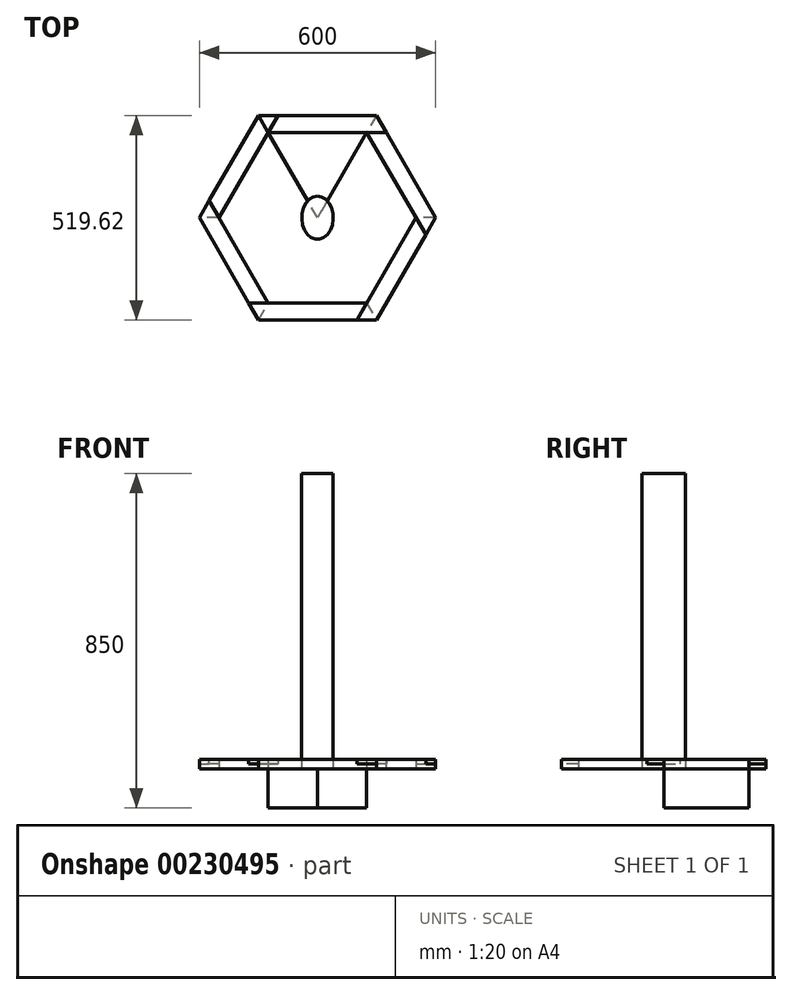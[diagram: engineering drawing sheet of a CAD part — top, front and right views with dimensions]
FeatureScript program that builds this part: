
annotation { "Feature Type Name" : "Feature", "Feature Type Description" : "" }
export const myFeature = defineFeature(function(context is Context, id is Id, definition is map)
    precondition{}
    {
        {
            var Q0;
            Q0=qCreatedBy(makeId("Top.planeOp"),FACE);
            var sketch = newSketch(context, id + "F0", { "sketchPlane" : qUnion([Q0])});
            skLineSegment(sketch, "E0", {"start": v(0, 0) * mm, "end": v(300, 0) * mm});
            skLineSegment(sketch, "E1", {"start": v(-24.83, 43) * mm, "end": v(275.17, 43) * mm});
            skLineSegment(sketch, "E2", {"start": v(0, 0) * mm, "end": v(-24.83, 43) * mm});
            skLineSegment(sketch, "E3", {"start": v(300, 0) * mm, "end": v(275.17, 43) * mm});
            skSolve(sketch);
        }
        {
            var Q0;
            Q0 = qSketchRegion(id + "F0", true);
            extrude(context, id + "F1", {"entities" : qUnion([Q0]), "depth" : 23 * mm});
        }
        {
            var Q0;
            Q0=makeQuery(id+"F1.opExtrude","CAP_FACE",FACE,{"disambiguationData":[OSD([sQuery(id+"F0.wireOp",EDGE,"E0"),sQuery(id+"F0.wireOp",EDGE,"E1"),sQuery(id+"F0.wireOp",EDGE,"E2"),sQuery(id+"F0.wireOp",EDGE,"E3")])],"isStart":false});
            var sketch = newSketch(context, id + "F2", { "sketchPlane" : qUnion([Q0])});
            skLineSegment(sketch, "E4", {"start": v(0, 0) * mm, "end": v(24.83, 43) * mm});
            skLineSegment(sketch, "E5", {"start": v(24.83, 43) * mm, "end": v(-24.83, 43) * mm});
            skLineSegment(sketch, "E6", {"start": v(-24.83, 43) * mm, "end": v(0, 0) * mm});
            skSolve(sketch);
        }
        {
            var Q0;
            Q0=makeQuery(id+"F2.imprint","IMPRINT",FACE,{"disambiguationData":[TD([[makeQuery(id+"F2.imprint","IMPRINT",EDGE,{"derivedFrom":sQuery(id+"F2.wireOp",EDGE,"E4")}),1.0]])]});
            extrude(context, id + "F3", {"entities" : qUnion([Q0]), "operationType" : NewBodyOperationType.REMOVE, "oppositeDirection" : true, "depth" : 11.5 * mm});
        }
        {
            var Q0;
            Q0=makeQuery(id+"F1.opExtrude","CAP_FACE",FACE,{"disambiguationData":[OSD([sQuery(id+"F0.wireOp",EDGE,"E0"),sQuery(id+"F0.wireOp",EDGE,"E1"),sQuery(id+"F0.wireOp",EDGE,"E2"),sQuery(id+"F0.wireOp",EDGE,"E3")])],"isStart":true});
            var sketch = newSketch(context, id + "F4", { "sketchPlane" : qUnion([Q0])});
            skLineSegment(sketch, "E7", {"start": v(275.17, -43) * mm, "end": v(250.35, 0) * mm});
            skLineSegment(sketch, "E8", {"start": v(250.35, 0) * mm, "end": v(300, 0) * mm});
            skLineSegment(sketch, "E9", {"start": v(300, 0) * mm, "end": v(275.17, -43) * mm});
            skSolve(sketch);
        }
        {
            var Q0;
            Q0=makeQuery(id+"F4.imprint","IMPRINT",FACE,{"disambiguationData":[TD([[makeQuery(id+"F4.imprint","IMPRINT",EDGE,{"derivedFrom":sQuery(id+"F4.wireOp",EDGE,"E7")}),-1.0]])]});
            extrude(context, id + "F5", {"entities" : qUnion([Q0]), "operationType" : NewBodyOperationType.REMOVE, "oppositeDirection" : true, "depth" : 11.5 * mm});
        }
        {
            var Q0;
            Q0=qCreatedBy(makeId("Top.planeOp"),FACE);
            var sketch = newSketch(context, id + "F6", { "sketchPlane" : qUnion([Q0])});
            skLineSegment(sketch, "E10", {"start": v(0, 0) * mm, "end": v(250.35, 0) * mm});
            skLineSegment(sketch, "E11", {"start": v(250.35, 0) * mm, "end": v(125.17, -216.8) * mm});
            skLineSegment(sketch, "E12", {"start": v(125.17, -216.8) * mm, "end": v(0, 0) * mm});
            skSolve(sketch);
        }
        {
            var Q0;
            Q0 = qSketchRegion(id + "F6", true);
            extrude(context, id + "F7", {"entities" : qUnion([Q0]), "oppositeDirection" : true, "depth" : 100 * mm});
        }
        {
            var Q0;
            Q0=makeQuery(id+"F1.opExtrude","SWEPT_BODY",BODY,{"disambiguationData":[OSD([sQuery(id+"F0.wireOp",EDGE,"E0"),sQuery(id+"F0.wireOp",EDGE,"E1"),sQuery(id+"F0.wireOp",EDGE,"E2"),sQuery(id+"F0.wireOp",EDGE,"E3")])]});
            var Q1;
            Q1=makeQuery(id+"F7.opExtrude","SWEPT_EDGE",EDGE,{"disambiguationData":[OSD([sQuery(id+"F6.wireOp",EDGE,"E11"),sQuery(id+"F6.wireOp",EDGE,"E12")])]});
            circularPattern(context, id + "F8", {"entities" : qUnion([Q0]), "axis" : qUnion([Q1]), "angle" : 360 * degree, "instanceCount" : 6, "equalSpace" : true});
        }
        {
            var Q0;
            Q0=makeQuery(id+"F8.opPattern","COPY",FACE,{"derivedFrom":makeQuery(id+"F1.opExtrude","CAP_FACE",FACE,{"disambiguationData":[OSD([sQuery(id+"F0.wireOp",EDGE,"E0"),sQuery(id+"F0.wireOp",EDGE,"E1"),sQuery(id+"F0.wireOp",EDGE,"E2"),sQuery(id+"F0.wireOp",EDGE,"E3")])],"isStart":true}),"instanceName":"3"});
            var sketch = newSketch(context, id + "F9", { "sketchPlane" : qUnion([Q0])});
            skLineSegment(sketch, "E13", {"start": v(105.17, 476.62) * mm, "end": v(105.17, 228.35) * mm});
            skLineSegment(sketch, "E14", {"start": v(105.17, 476.62) * mm, "end": v(145.17, 476.62) * mm});
            skLineSegment(sketch, "E15", {"start": v(145.17, 476.62) * mm, "end": v(145.17, 228.35) * mm});
            skLineSegment(sketch, "E16", {"start": v(-62.59, 325.21) * mm, "end": v(312.93, 108.4) * mm, "construction": true});
            skLineSegment(sketch, "E17.MirrorCS", {"start": v(-89.83, 69.58) * mm, "end": v(125.17, 193.71) * mm});
            skLineSegment(sketch, "E18.MirrorCS", {"start": v(-109.83, 104.22) * mm, "end": v(-89.83, 69.58) * mm});
            skLineSegment(sketch, "E19.MirrorCS", {"start": v(-109.83, 104.22) * mm, "end": v(105.17, 228.35) * mm});
            skLineSegment(sketch, "E20", {"start": v(-62.59, 108.4) * mm, "end": v(312.93, 325.21) * mm, "construction": true});
            skLineSegment(sketch, "E21.MirrorCS", {"start": v(340.17, 69.58) * mm, "end": v(360.17, 104.22) * mm});
            skLineSegment(sketch, "E22.MirrorCS", {"start": v(340.17, 69.58) * mm, "end": v(125.17, 193.71) * mm});
            skLineSegment(sketch, "E23.MirrorCS", {"start": v(360.17, 104.22) * mm, "end": v(145.17, 228.35) * mm});
            skPoint(sketch, "E24", {"position": v(125.17, 216.8) * mm});
            skLineSegment(sketch, "E25", {"start": v(105.17, 228.35) * mm, "end": v(125.17, 216.8) * mm});
            skLineSegment(sketch, "E26", {"start": v(125.17, 216.8) * mm, "end": v(125.17, 193.71) * mm});
            skLineSegment(sketch, "E27", {"start": v(125.17, 216.8) * mm, "end": v(145.17, 228.35) * mm});
            skEllipse(sketch, "E28", {"center": v(125.17, 216.8) * mm, "majorRadius": 55 * mm, "minorRadius": 40 * mm, "majorAxis": v(0, -1)});
            skLineSegment(sketch, "E29", {"start": v(125.17, 161.8) * mm, "end": v(125.17, 271.8) * mm, "construction": true});
            skLineSegment(sketch, "E30", {"start": v(125.17, 433.62) * mm, "end": v(125.17, 0) * mm, "construction": true});
            skSolve(sketch);
        }
        {
            var Q0;
            {var subQ1=sQuery(id+"F9.wireOp",EDGE,"E13");var subQ3=sQuery(id+"F9.wireOp",EDGE,"E28");var subQ4=makeQuery(id+"F9.imprint","INTERSECT",VERTEX,{"derivedFrom":[subQ1,subQ3]});Q0=makeQuery(id+"F9.imprint","IMPRINT",FACE,{"disambiguationData":[TD([[makeQuery(id+"F9.imprint","IMPRINT",EDGE,{"disambiguationData":[TD([[subQ4,-1.0]])],"derivedFrom":subQ3}),1.0]])]});}
            var Q1;
            {var subQ6=sQuery(id+"F9.wireOp",EDGE,"E25");Q1=makeQuery(id+"F9.imprint","IMPRINT",FACE,{"disambiguationData":[TD([[makeQuery(id+"F9.imprint","IMPRINT",EDGE,{"derivedFrom":subQ6}),1.0]])]});}
            var Q2;
            {var subQ1=sQuery(id+"F9.wireOp",EDGE,"E25");Q2=makeQuery(id+"F9.imprint","IMPRINT",FACE,{"disambiguationData":[TD([[makeQuery(id+"F9.imprint","IMPRINT",EDGE,{"derivedFrom":subQ1}),-1.0]])]});}
            var Q3;
            {var subQ1=sQuery(id+"F9.wireOp",EDGE,"E17.MirrorCS");var subQ3=sQuery(id+"F9.wireOp",EDGE,"E28");var subQ4=makeQuery(id+"F9.imprint","INTERSECT",VERTEX,{"derivedFrom":[subQ1,subQ3]});Q3=makeQuery(id+"F9.imprint","IMPRINT",FACE,{"disambiguationData":[TD([[makeQuery(id+"F9.imprint","IMPRINT",EDGE,{"disambiguationData":[TD([[subQ4,-1.0]])],"derivedFrom":subQ3}),1.0]])]});}
            var Q4;
            {var subQ1=sQuery(id+"F9.wireOp",EDGE,"E26");Q4=makeQuery(id+"F9.imprint","IMPRINT",FACE,{"disambiguationData":[TD([[makeQuery(id+"F9.imprint","IMPRINT",EDGE,{"derivedFrom":subQ1}),1.0]])]});}
            var Q5;
            {var subQ1=sQuery(id+"F9.wireOp",EDGE,"E15");var subQ3=sQuery(id+"F9.wireOp",EDGE,"E28");var subQ4=makeQuery(id+"F9.imprint","INTERSECT",VERTEX,{"derivedFrom":[subQ1,subQ3]});Q5=makeQuery(id+"F9.imprint","IMPRINT",FACE,{"disambiguationData":[TD([[makeQuery(id+"F9.imprint","IMPRINT",EDGE,{"disambiguationData":[TD([[subQ4,1.0]])],"derivedFrom":subQ3}),1.0]])]});}
            var Q6;
            Q6=sQuery(id+"F9.wireOp",EDGE,"E28");
            extrude(context, id + "F10", {"entities" : qUnion([Q0, Q1, Q2, Q3, Q4, Q5]), "surfaceEntities" : qUnion([Q6]), "oppositeDirection" : true, "depth" : 750 * mm});
        }
    });
